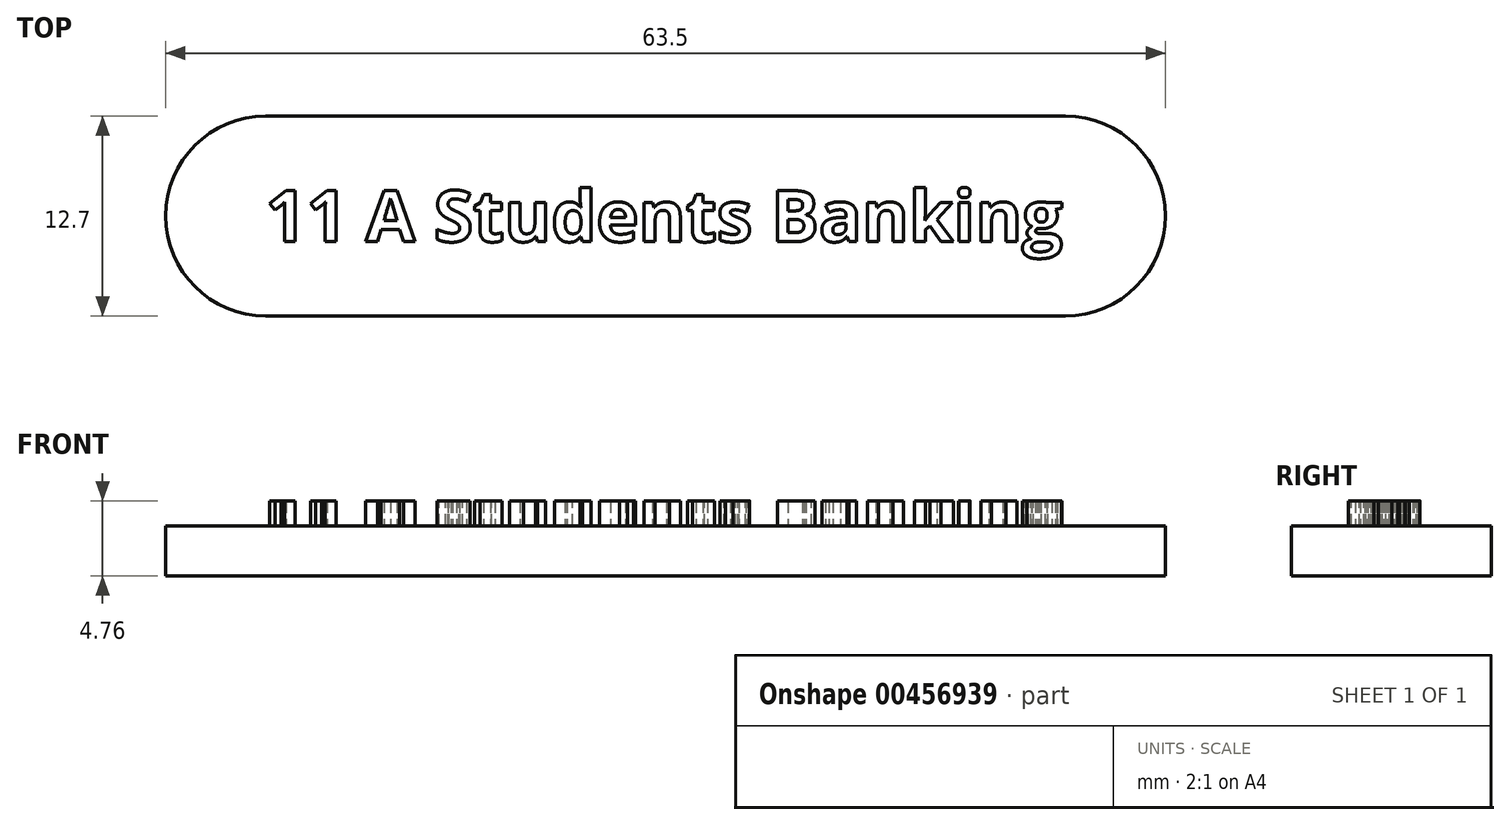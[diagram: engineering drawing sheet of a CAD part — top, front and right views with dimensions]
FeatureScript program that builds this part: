
annotation { "Feature Type Name" : "Feature", "Feature Type Description" : "" }
export const myFeature = defineFeature(function(context is Context, id is Id, definition is map)
    precondition{}
    {
        {
            var Q0;
            Q0=qCreatedBy(makeId("Top.planeOp"),FACE);
            var sketch = newSketch(context, id + "F0", { "sketchPlane" : qUnion([Q0])});
            skLineSegment(sketch, "E0.bottom", {"start": v(25.4, 6.35) * mm, "end": v(-25.4, 6.35) * mm});
            skLineSegment(sketch, "E0.top", {"start": v(25.4, -6.35) * mm, "end": v(-25.4, -6.35) * mm});
            skLineSegment(sketch, "E0.left", {"start": v(25.4, 6.35) * mm, "end": v(25.4, -6.35) * mm, "construction": true});
            skLineSegment(sketch, "E0.right", {"start": v(-25.4, 6.35) * mm, "end": v(-25.4, -6.35) * mm, "construction": true});
            skPoint(sketch, "E0.middle", {"position": v(0, 0) * mm});
            skArc(sketch, "E1", {"start": v(-25.4, 6.35) * mm, "mid": v(-31.75, 0) * mm, "end": v(-25.4, -6.35) * mm});
            skArc(sketch, "E2", {"start": v(25.4, -6.35) * mm, "mid": v(31.75, 0) * mm, "end": v(25.4, 6.35) * mm});
            skSolve(sketch);
        }
        {
            var Q0;
            Q0=qSketchRegion(id+"F0",true);
            extrude(context, id + "F1", {"entities" : qUnion([Q0]), "depth" : 3.17 * mm});
        }
        {
            var Q0;
            Q0=makeQuery(id+"F1.opExtrude","CAP_FACE",FACE,{"disambiguationData":[OSD([sQuery(id+"F0.wireOp",EDGE,"E0.bottom"),sQuery(id+"F0.wireOp",EDGE,"E0.top"),sQuery(id+"F0.wireOp",EDGE,"E1"),sQuery(id+"F0.wireOp",EDGE,"E2")])],"isStart":false});
            var sketch = newSketch(context, id + "F2", { "sketchPlane" : qUnion([Q0])});
            skText(sketch, "E3", { "text": "11 A Students Banking", "fontName": "OpenSans-Bold.ttf"});
            const initialGuessF2  = {"E3": [-0.0254, -0.00163, 1, 0, 0.00327]};
            skSetInitialGuess(sketch, initialGuessF2);
            skSolve(sketch);
        }
        {
            var Q0;
            Q0=qSketchRegion(id+"F2",true);
            extrude(context, id + "F3", {"entities" : qUnion([Q0]), "operationType" : NewBodyOperationType.ADD, "depth" : 1.59 * mm});
        }
    });
